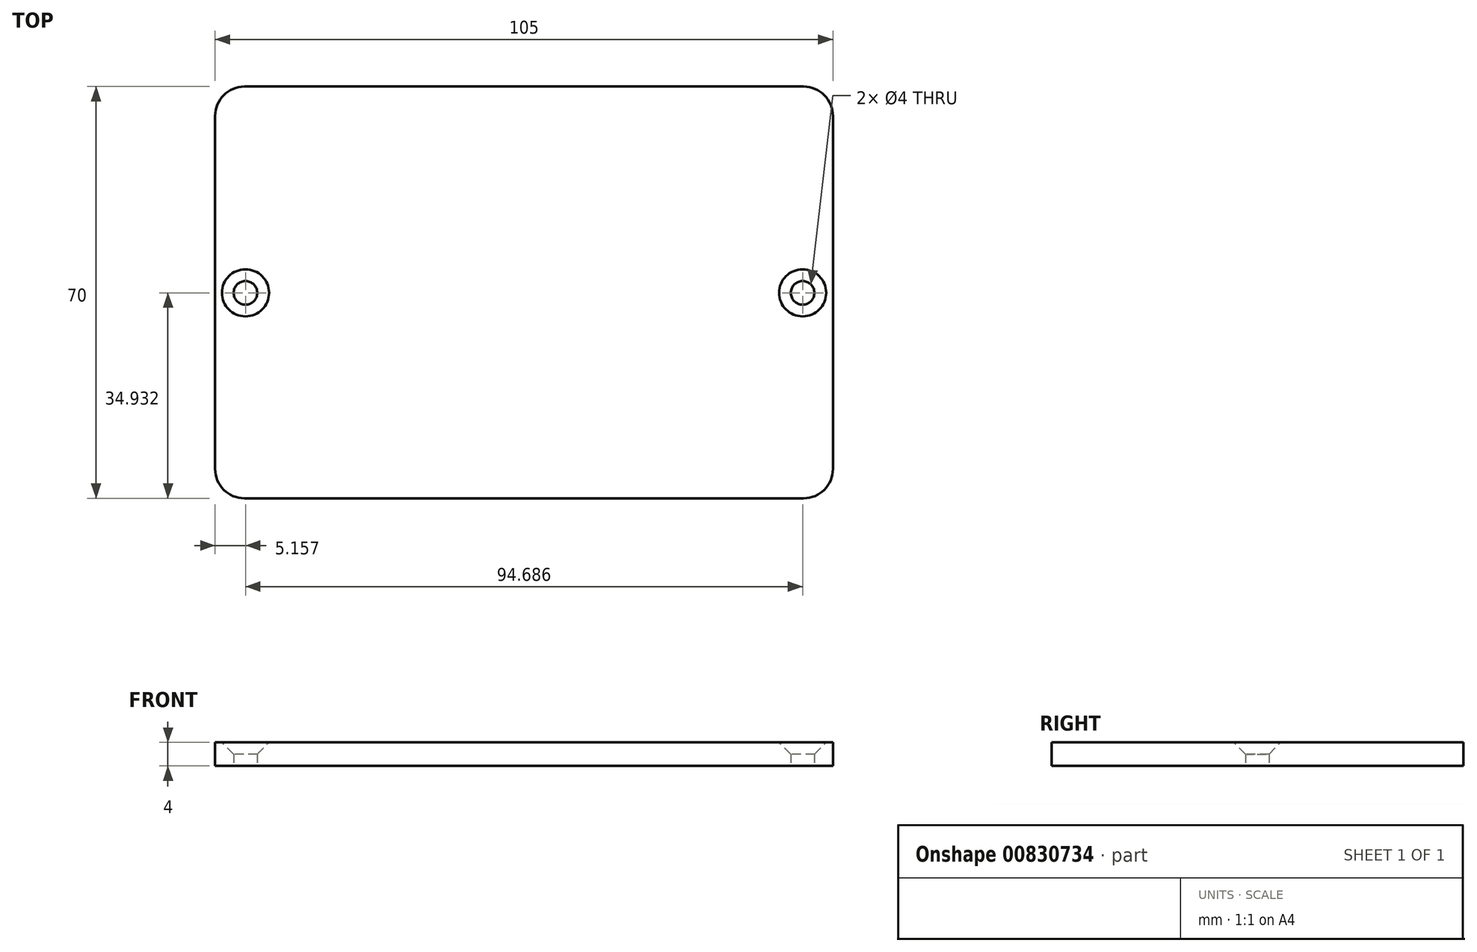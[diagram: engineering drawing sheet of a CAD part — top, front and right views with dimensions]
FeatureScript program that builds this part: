
annotation { "Feature Type Name" : "Feature", "Feature Type Description" : "" }
export const myFeature = defineFeature(function(context is Context, id is Id, definition is map)
    precondition{}
    {
        {
            var Q0;
            Q0=qCreatedBy(makeId("Top.planeOp"),FACE);
            var sketch = newSketch(context, id + "F0", { "sketchPlane" : qUnion([Q0])});
            skLineSegment(sketch, "E0.bottom", {"start": v(47.5, -35) * mm, "end": v(-47.5, -35) * mm});
            skLineSegment(sketch, "E0.top", {"start": v(47.5, 35) * mm, "end": v(-47.5, 35) * mm});
            skLineSegment(sketch, "E0.left", {"start": v(52.5, -30) * mm, "end": v(52.5, 30) * mm});
            skLineSegment(sketch, "E0.right", {"start": v(-52.5, -30) * mm, "end": v(-52.5, 30) * mm});
            skPoint(sketch, "E0.middle", {"position": v(0, 0) * mm});
            skPoint(sketch, "E1.visualSharp", {"position": v(-52.5, 35) * mm});
            skArc(sketch, "E1.filletArc", {"start": v(-47.5, 35) * mm, "mid": v(-51.04, 33.54) * mm, "end": v(-52.5, 30) * mm});
            skPoint(sketch, "E2.visualSharp", {"position": v(52.5, 35) * mm});
            skArc(sketch, "E2.filletArc", {"start": v(52.5, 30) * mm, "mid": v(51.04, 33.54) * mm, "end": v(47.5, 35) * mm});
            skPoint(sketch, "E3.visualSharp", {"position": v(52.5, -35) * mm});
            skArc(sketch, "E3.filletArc", {"start": v(47.5, -35) * mm, "mid": v(51.04, -33.54) * mm, "end": v(52.5, -30) * mm});
            skPoint(sketch, "E4.visualSharp", {"position": v(-52.5, -35) * mm});
            skArc(sketch, "E4.filletArc", {"start": v(-52.5, -30) * mm, "mid": v(-51.04, -33.54) * mm, "end": v(-47.5, -35) * mm});
            skCircle(sketch, "E5", {"center": v(-47.34, -0.07) * mm, "radius": 2 * mm});
            skLineSegment(sketch, "E6", {"start": v(0, 74.91) * mm, "end": v(0, -44.14) * mm, "construction": true});
            skPoint(sketch, "E6.endSnap0", {"position": v(0, -35) * mm});
            skCircle(sketch, "E7.MirrorC", {"center": v(47.34, -0.07) * mm, "radius": 2 * mm});
            skLineSegment(sketch, "E8", {"start": v(-75.73, 0) * mm, "end": v(90.36, 0) * mm, "construction": true});
            skSolve(sketch);
        }
        {
            var Q0;
            Q0 = qSketchRegion(id + "F0", true);
            extrude(context, id + "F1", {"entities" : qUnion([Q0]), "depth" : 4 * mm, "offsetDistance" : 25 * mm});
        }
        {
            var Q0;
            Q0=makeQuery(id+"F1.opExtrude","CAP_EDGE",EDGE,{"disambiguationData":[OSD([sQuery(id+"F0.wireOp",EDGE,"E5")])],"isStart":false});
            var Q1;
            Q1=makeQuery(id+"F1.opExtrude","CAP_EDGE",EDGE,{"disambiguationData":[OSD([sQuery(id+"F0.wireOp",EDGE,"E7.MirrorC")])],"isStart":false});
            chamfer(context, id + "F2", {"entities" : qUnion([Q0, Q1]), "width" : 2 * mm, "tangentPropagation" : true});
        }
    });
